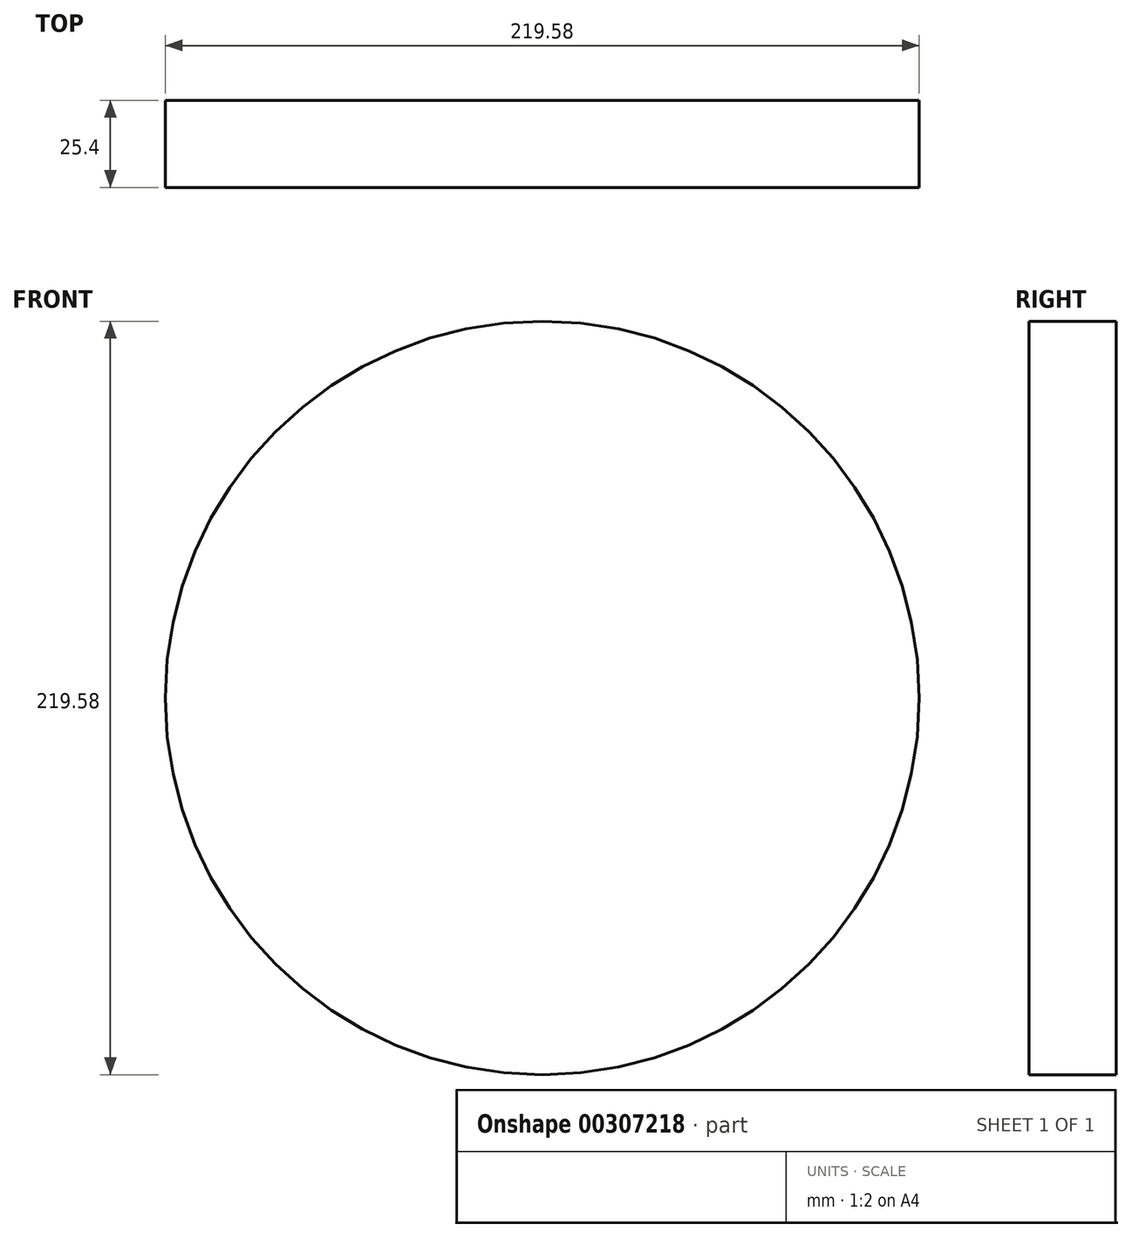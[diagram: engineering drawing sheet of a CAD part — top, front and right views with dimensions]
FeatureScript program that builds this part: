
annotation { "Feature Type Name" : "Feature", "Feature Type Description" : "" }
export const myFeature = defineFeature(function(context is Context, id is Id, definition is map)
    precondition{}
    {
        {
            var Q0;
            Q0=qCreatedBy(makeId("Front.planeOp"),FACE);
            var sketch = newSketch(context, id + "F0", { "sketchPlane" : qUnion([Q0])});
            skCircle(sketch, "E0", {"center": v(34.57, 0) * mm, "radius": 109.8 * mm});
            skCircle(sketch, "E1", {"center": v(34.57, -60.82) * mm, "radius": 50.86 * mm});
            skCircle(sketch, "E2", {"center": v(34.57, 44.57) * mm, "radius": 43.73 * mm});
            skSolve(sketch);
        }
        {
            var Q0;
            Q0=sQuery(id+"F0.wireOp",EDGE,"E0");
            extrude(context, id + "F1", {"bodyType" : ToolBodyType.SURFACE, "surfaceEntities" : qUnion([Q0]), "depth" : 25.4 * mm});
        }
    });
